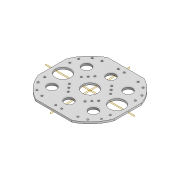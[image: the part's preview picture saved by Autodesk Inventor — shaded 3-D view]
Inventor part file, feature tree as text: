
AUTODESK INVENTOR PART (.ipt)
format: ipt  version: 2022 (Build 260153000, 153)  size: 235,008 bytes
history: native  units: mm
features: extrude x3, mirror x3, plane x2, sketch x2, projected_geometry x1
ambient origin geometry x8: Origin, YZ Plane, XZ Plane, XY Plane, X Axis, Y Axis, Z Axis, Center Point
bodies: Solid1 (feature_tree)
feature tree (11):
  extrude  "Extrusion1"  Depth=3.0mm TaperAngle=0.0deg
  extrude  "Extrusion3"  Depth=10.0mm
  plane  "Work Plane5"
  plane  "Work Plane6"
  mirror  "Mirror3"
  mirror  "Mirror4"
  extrude  "Extrusion4"  Depth=3.0mm
  mirror  "Mirror5"
  sketch  "Sketch10"  dims[d25=60.0mm d27=8.726646mm d28=3.0mm d30=3.0mm d32=25.0mm d33=62.0mm d34=8.0mm d35=8.0mm d36=10.0mm d37=0.0mm d38=63.0mm d39=63.0mm d40=3.0mm d41=25.0mm d42=3.0mm d43=3.0mm d44=8.0mm d45=8.0mm d46=4.95mm d47=4.95mm d48=100.0mm d49=0.0mm d50=3.0mm d51=10.0mm d52=25.0mm d53=45.0mm d54=15.0mm d55=35.0mm d56=15.0mm d57=45.0mm d58=25.0mm]
  sketch  "Sketch7"  dims[d0=120.0mm d2=3.0mm d3=0.0mm]
  projected_geometry  "Projected Loop6"
